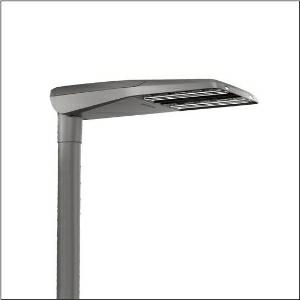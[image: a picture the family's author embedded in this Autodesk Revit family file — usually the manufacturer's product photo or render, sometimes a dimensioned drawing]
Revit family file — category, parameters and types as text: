
# Revit family: streetlight_sl_11_iq_midi___st0_5st0_5_5xc3h41f08me_a774
name_source: partatom
category: Lighting Fixtures
units: mm (PartAtom-declared; Revit-internal decimal feet)

## family parameters
Cut with Voids When Loaded = No
Host = Face
Light Source = No
Part Type = Normal
Room Calculation Point = No
Round Connector Dimension = Use Diameter
Shared = No

## types (1)
- --- (1 x LED, 18720 lm, 124.7 W, 4000K)
    Apparent Load = 125 VA
    CIE Flux Codes = 43 74 97 100 100
    Color Rendering = 70
    Color Temperature = 4000K
    Default Elevation = 1800 mm
    Description = Streetlight SL 11 iQ midi, mast luminaire, primary light control with 3 zone facetted reflector, of plastic, silver coated, highly specular, primary optical cover: cover, of PMMA, transparent, light distribution: ST0.5ST0.5, light emission: direct distribution, primary light characteristic: asymmetric, installation type: post-top, side-entry, LED, High Power LED, rated luminous flux: 18.720lm, luminous efficacy: 150lm/W, light colour: 740, colour temperature: 4000K, control: Street-Remote, optimised constant luminous flux control (CLO 2.0), Desk-Remote (wireless, voltage-free reading and setting of iQ features in the workshop via application-optimized NFC function/RFID function), Light-Fading, Smart-Wire, Night-Set, Lumen-Switch, Temp-Guard, Auto-Match, with cable H07RN-F 5x 1.5mm², mains connection: 220..240V, AC, 50/60Hz, connection cable pre-assembled, cable length: 12,5m, start of lifetime: 125W, end of lifetime: 132W, reduction: 57W, luminaire housing, of diecast aluminium, powder-coated, Siteco® metallic grey (DB 702S), length: 780mm, width: 376mm, height: 118mm, spigot size: 60/76mm (post-top) and 42/60/76mm (side-entry), mast flange for spigot size: 42mm: 5XC10008XM4, 60mm: 5XC10008XM2, 76/60mm: 5XC10108XM1, equipment: Power, protection rating (complete): IP66, insulation class (complete): insulation class II (safety insulation), certification: CE, ENEC, VDE, impact resistance: IK09, permissible operating ambient temperature for outdoor applications: -25..+50°C, standard-compliant lighting for roads and squares, packaging unit: 1 piece

Light Distribution: ST0.5ST0.5
    Height = 118 mm
    Lamp = 1 x LED
    Lamp Light Flux = 18720 lm
    Lamp Power = 124.7 W
    Lamp count = 1
    Length = 780 mm
    Luminous efficacy = 150 lm/W
    Manufacturer = Siteco
    ModVariant = No
    Model = 5XC3H41F08ME
    Number of Poles = 1
    OnlyDefault = Yes
    Power Factor = 1
    Product Name = Streetlight SL 11 iQ midi | ST0.5ST0.5
    Product group = mast luminaire | pylon top
    ProductGroupID = 6100
    Protection Class = Protection class II
    Protection Degree = IP 66
    RLX_Detail_Level = 1
    RlxData = <blob elided: 75093 chars, md5=62fb3b21>
    Socket = socket
    Standby Power = 0 W
    System Light Flux = 18720 lm
    System Power = 125 W
    Type Comments = factory setting: luminous flux: 100 % | dim-lin: 254 | 557 mA
    Type Image = l_1005960.jpg
    URL = http://relux.com
    VarID = @adj_086513
    Voltage = 0 V
    Weight = 0.00 kg
    Width = 376 mm

## geometry (parser evidence)
native form markers: Blend x4, Sweep x9
no freeform markers — native parametric forms only
